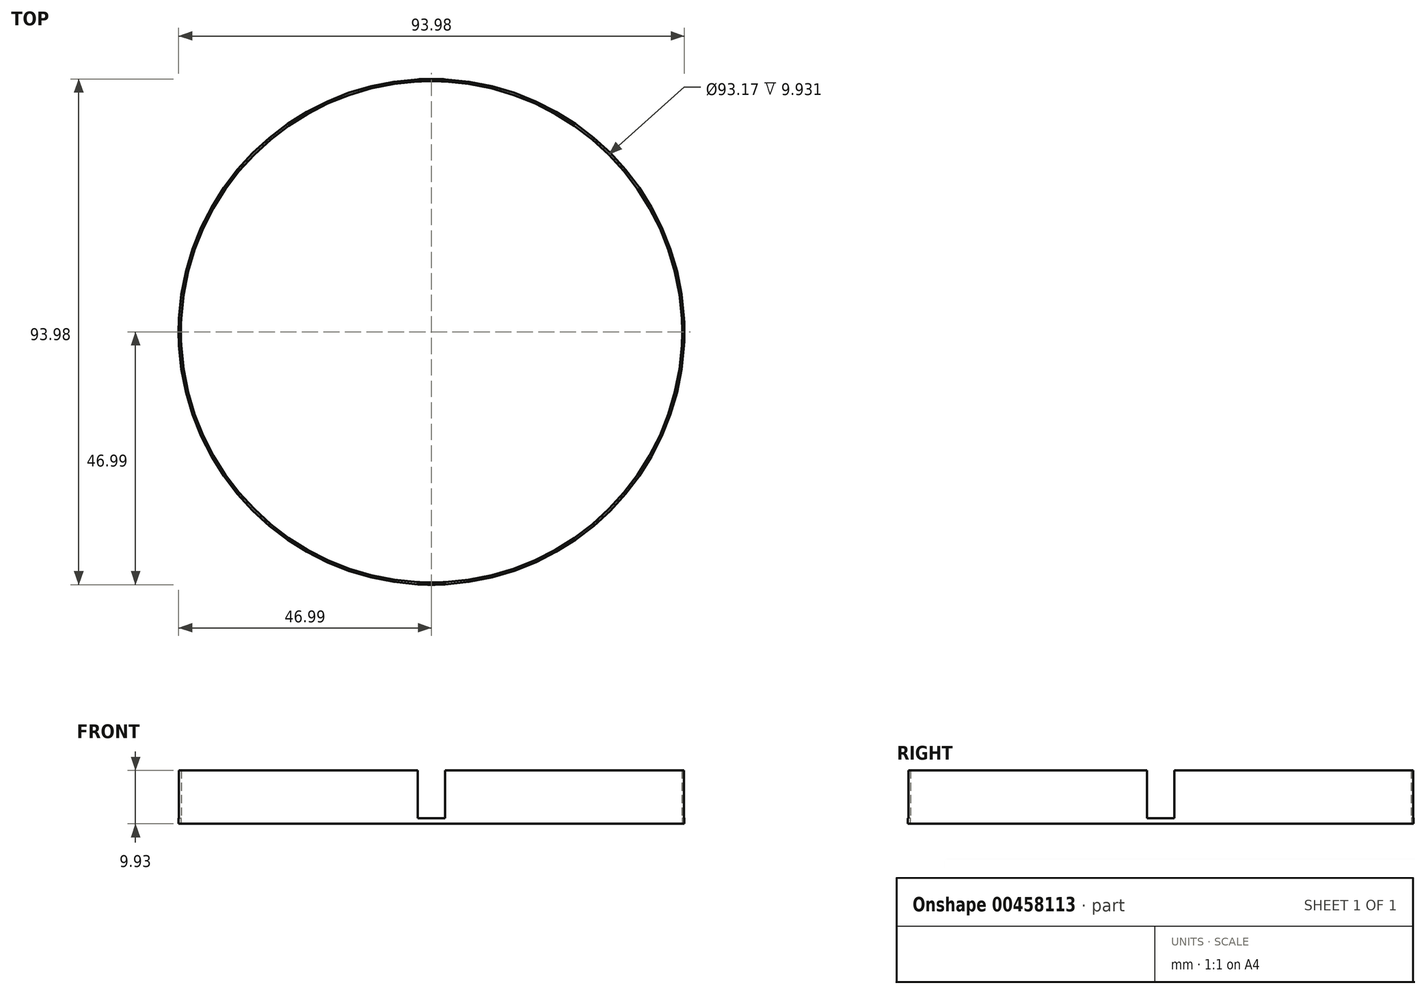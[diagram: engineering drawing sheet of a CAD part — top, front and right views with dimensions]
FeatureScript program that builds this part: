
annotation { "Feature Type Name" : "Feature", "Feature Type Description" : "" }
export const myFeature = defineFeature(function(context is Context, id is Id, definition is map)
    precondition{}
    {
        {
            var Q0;
            Q0=qCreatedBy(makeId("Top.planeOp"),FACE);
            var sketch = newSketch(context, id + "F0", { "sketchPlane" : qUnion([Q0])});
            skCircle(sketch, "E0", {"center": v(0, 0) * mm, "radius": 47 * mm});
            skCircle(sketch, "E1", {"center": v(0, 0) * mm, "radius": 46.58 * mm});
            skSolve(sketch);
        }
        {
            var Q0;
            Q0=makeQuery(id+"F0.imprint","IMPRINT",FACE,{"disambiguationData":[TD([[makeQuery(id+"F0.imprint","IMPRINT",EDGE,{"derivedFrom":sQuery(id+"F0.wireOp",EDGE,"E0")}),1.0]])]});
            extrude(context, id + "F1", {"entities" : qUnion([Q0]), "depth" : 9.93 * mm});
        }
        {
            var Q0;
            Q0=qCreatedBy(makeId("Right.planeOp"),FACE);
            var sketch = newSketch(context, id + "F2", { "sketchPlane" : qUnion([Q0])});
            skLineSegment(sketch, "E2.bottom", {"start": v(-2.54, 1.05) * mm, "end": v(2.54, 1.05) * mm});
            skLineSegment(sketch, "E2.top", {"start": v(-2.54, 13.75) * mm, "end": v(2.54, 13.75) * mm});
            skLineSegment(sketch, "E2.left", {"start": v(-2.54, 1.05) * mm, "end": v(-2.54, 13.75) * mm});
            skLineSegment(sketch, "E2.right", {"start": v(2.54, 1.05) * mm, "end": v(2.54, 13.75) * mm});
            skSolve(sketch);
        }
        {
            var Q0;
            Q0=makeQuery(id+"F2.imprint","IMPRINT",FACE,{"disambiguationData":[TD([[makeQuery(id+"F2.imprint","IMPRINT",EDGE,{"derivedFrom":sQuery(id+"F2.wireOp",EDGE,"E2.bottom")}),1.0]])]});
            extrude(context, id + "F3", {"entities" : qUnion([Q0]), "operationType" : NewBodyOperationType.REMOVE, "endBound" : BoundingType.SYMMETRIC, "oppositeDirection" : true, "depth" : 152.4 * mm});
        }
        {
            var Q0;
            Q0=qCreatedBy(makeId("Front.planeOp"),FACE);
            var sketch = newSketch(context, id + "F4", { "sketchPlane" : qUnion([Q0])});
            skLineSegment(sketch, "E3.bottom", {"start": v(-2.54, 1.05) * mm, "end": v(2.54, 1.05) * mm});
            skLineSegment(sketch, "E3.top", {"start": v(-2.54, 13.75) * mm, "end": v(2.54, 13.75) * mm});
            skLineSegment(sketch, "E3.left", {"start": v(-2.54, 1.05) * mm, "end": v(-2.54, 13.75) * mm});
            skLineSegment(sketch, "E3.right", {"start": v(2.54, 1.05) * mm, "end": v(2.54, 13.75) * mm});
            skSolve(sketch);
        }
        {
            var Q0;
            Q0=makeQuery(id+"F4.imprint","IMPRINT",FACE,{"disambiguationData":[TD([[makeQuery(id+"F4.imprint","IMPRINT",EDGE,{"derivedFrom":sQuery(id+"F4.wireOp",EDGE,"E3.bottom")}),1.0]])]});
            extrude(context, id + "F5", {"entities" : qUnion([Q0]), "operationType" : NewBodyOperationType.REMOVE, "endBound" : BoundingType.SYMMETRIC, "oppositeDirection" : true, "depth" : 152.4 * mm});
        }
    });
